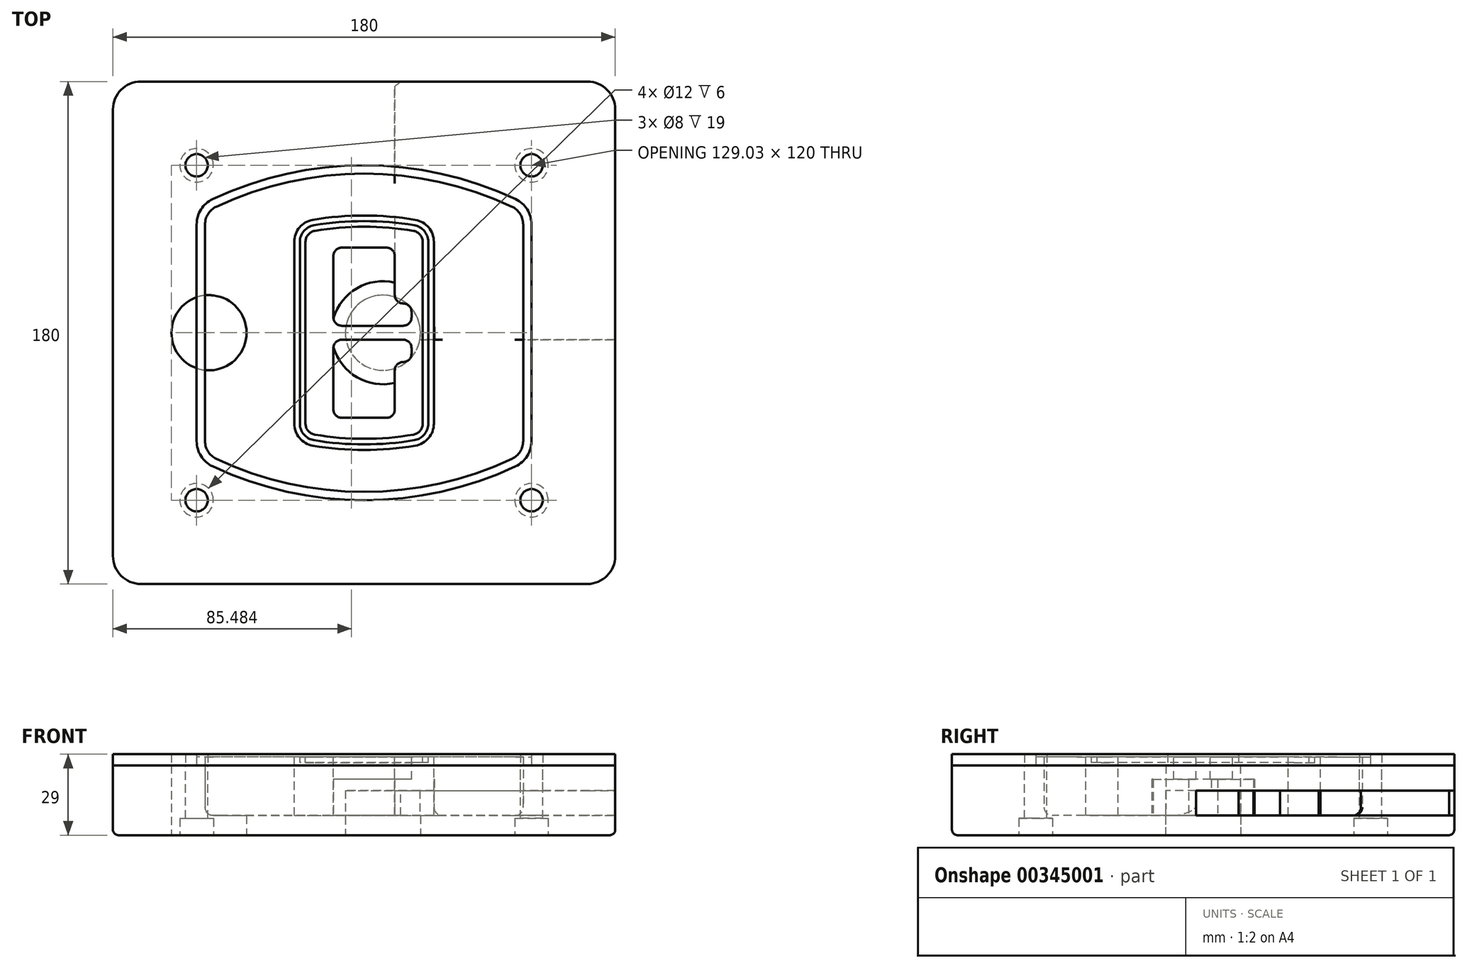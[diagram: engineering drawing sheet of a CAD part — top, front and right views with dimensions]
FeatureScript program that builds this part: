
annotation { "Feature Type Name" : "Feature", "Feature Type Description" : "" }
export const myFeature = defineFeature(function(context is Context, id is Id, definition is map)
    precondition{}
    {
        {
            var Q0;
            Q0=qCreatedBy(makeId("Top.planeOp"),FACE);
            var sketch = newSketch(context, id + "F0", { "sketchPlane" : qUnion([Q0])});
            skPoint(sketch, "E0.rect.middle", {"position": v(0, 0) * mm});
            skLineSegment(sketch, "E1.bottom", {"start": v(-80, -90) * mm, "end": v(80, -90) * mm});
            skLineSegment(sketch, "E1.top", {"start": v(-80, 90) * mm, "end": v(80, 90) * mm});
            skLineSegment(sketch, "E1.left", {"start": v(-90, -80) * mm, "end": v(-90, 80) * mm});
            skLineSegment(sketch, "E1.right", {"start": v(90, -80) * mm, "end": v(90, 80) * mm});
            skLineSegment(sketch, "E2", {"start": v(-90, 90) * mm, "end": v(90, -90) * mm, "construction": true});
            skLineSegment(sketch, "E3", {"start": v(90, 90) * mm, "end": v(-90, -90) * mm, "construction": true});
            skCircle(sketch, "E4", {"center": v(-60, 60) * mm, "radius": 4 * mm});
            skCircle(sketch, "E5", {"center": v(60, 60) * mm, "radius": 4 * mm});
            skCircle(sketch, "E6", {"center": v(60, -60) * mm, "radius": 4 * mm});
            skCircle(sketch, "E7", {"center": v(-60, -60) * mm, "radius": 4 * mm});
            skLineSegment(sketch, "E8", {"start": v(-60, 60) * mm, "end": v(60, 60) * mm, "construction": true});
            skLineSegment(sketch, "E9", {"start": v(60, 60) * mm, "end": v(60, -60) * mm, "construction": true});
            skLineSegment(sketch, "E10", {"start": v(60, -60) * mm, "end": v(-60, -60) * mm, "construction": true});
            skLineSegment(sketch, "E11", {"start": v(-60, -60) * mm, "end": v(-60, 60) * mm, "construction": true});
            skLineSegment(sketch, "E12", {"start": v(-60, 38.83) * mm, "end": v(-60, -38.83) * mm});
            skLineSegment(sketch, "E13", {"start": v(60, 38.83) * mm, "end": v(60, -38.83) * mm});
            skArc(sketch, "E14", {"start": v(54.26, 47.88) * mm, "mid": v(0, 60) * mm, "end": v(-54.26, 47.88) * mm});
            skArc(sketch, "E15", {"start": v(-54.26, -47.88) * mm, "mid": v(0, -60) * mm, "end": v(54.26, -47.88) * mm});
            skLineSegment(sketch, "E16", {"start": v(-60, 0) * mm, "end": v(60, 0) * mm, "construction": true});
            skPoint(sketch, "E17.visualSharp", {"position": v(-60, -45) * mm});
            skArc(sketch, "E17.filletArc", {"start": v(-60, -38.83) * mm, "mid": v(-58.44, -44.2) * mm, "end": v(-54.26, -47.88) * mm});
            skPoint(sketch, "E18.visualSharp", {"position": v(-60, 45) * mm});
            skArc(sketch, "E18.filletArc", {"start": v(-54.26, 47.88) * mm, "mid": v(-58.44, 44.2) * mm, "end": v(-60, 38.83) * mm});
            skPoint(sketch, "E19.visualSharp", {"position": v(60, 45) * mm});
            skArc(sketch, "E19.filletArc", {"start": v(60, 38.83) * mm, "mid": v(58.44, 44.2) * mm, "end": v(54.26, 47.88) * mm});
            skPoint(sketch, "E20.visualSharp", {"position": v(60, -45) * mm});
            skArc(sketch, "E20.filletArc", {"start": v(54.26, -47.88) * mm, "mid": v(58.44, -44.2) * mm, "end": v(60, -38.83) * mm});
            skPoint(sketch, "E21.visualSharp", {"position": v(-90, 90) * mm});
            skArc(sketch, "E21.filletArc", {"start": v(-80, 90) * mm, "mid": v(-87.07, 87.07) * mm, "end": v(-90, 80) * mm});
            skPoint(sketch, "E22.visualSharp", {"position": v(90, 90) * mm});
            skArc(sketch, "E22.filletArc", {"start": v(90, 80) * mm, "mid": v(87.07, 87.07) * mm, "end": v(80, 90) * mm});
            skPoint(sketch, "E23.visualSharp", {"position": v(90, -90) * mm});
            skArc(sketch, "E23.filletArc", {"start": v(80, -90) * mm, "mid": v(87.07, -87.07) * mm, "end": v(90, -80) * mm});
            skPoint(sketch, "E24.visualSharp", {"position": v(-90, -90) * mm});
            skArc(sketch, "E24.filletArc", {"start": v(-90, -80) * mm, "mid": v(-87.07, -87.07) * mm, "end": v(-80, -90) * mm});
            skArc(sketch, "E25.0", {"start": v(57, 38.83) * mm, "mid": v(55.9, 42.58) * mm, "end": v(52.98, 45.17) * mm});
            skLineSegment(sketch, "E25.1", {"start": v(57, 38.83) * mm, "end": v(57, -38.83) * mm});
            skArc(sketch, "E25.2", {"start": v(52.98, -45.17) * mm, "mid": v(55.9, -42.58) * mm, "end": v(57, -38.83) * mm});
            skArc(sketch, "E25.3", {"start": v(-52.98, -45.17) * mm, "mid": v(0, -57) * mm, "end": v(52.98, -45.17) * mm});
            skArc(sketch, "E25.4", {"start": v(-57, -38.83) * mm, "mid": v(-55.9, -42.58) * mm, "end": v(-52.98, -45.17) * mm});
            skArc(sketch, "E25.5", {"start": v(52.98, 45.17) * mm, "mid": v(0, 57) * mm, "end": v(-52.98, 45.17) * mm});
            skLineSegment(sketch, "E25.6", {"start": v(-57, 38.83) * mm, "end": v(-57, -38.83) * mm});
            skArc(sketch, "E25.7", {"start": v(-52.98, 45.17) * mm, "mid": v(-55.9, 42.58) * mm, "end": v(-57, 38.83) * mm});
            skArc(sketch, "E26.0", {"start": v(-55.96, 51.5) * mm, "mid": v(-61.82, 46.33) * mm, "end": v(-64, 38.83) * mm});
            skArc(sketch, "E26.1", {"start": v(55.96, 51.5) * mm, "mid": v(0, 64) * mm, "end": v(-55.96, 51.5) * mm});
            skArc(sketch, "E26.2", {"start": v(64, 38.83) * mm, "mid": v(61.82, 46.33) * mm, "end": v(55.96, 51.5) * mm});
            skLineSegment(sketch, "E26.3", {"start": v(64, 38.83) * mm, "end": v(64, -38.83) * mm});
            skArc(sketch, "E26.4", {"start": v(55.96, -51.5) * mm, "mid": v(61.82, -46.33) * mm, "end": v(64, -38.83) * mm});
            skLineSegment(sketch, "E26.5", {"start": v(-64, 38.83) * mm, "end": v(-64, -38.83) * mm});
            skArc(sketch, "E26.6", {"start": v(-55.96, -51.5) * mm, "mid": v(0, -64) * mm, "end": v(55.96, -51.5) * mm});
            skArc(sketch, "E26.7", {"start": v(-64, -38.83) * mm, "mid": v(-61.82, -46.33) * mm, "end": v(-55.96, -51.5) * mm});
            skSolve(sketch);
        }
        {
            var Q0;
            Q0=makeQuery(id+"F0.imprint","IMPRINT",FACE,{"disambiguationData":[TD([[makeQuery(id+"F0.imprint","IMPRINT",EDGE,{"derivedFrom":sQuery(id+"F0.wireOp",EDGE,"E1.bottom")}),1.0]])]});
            var Q1;
            Q1=makeQuery(id+"F0.imprint","IMPRINT",FACE,{"disambiguationData":[TD([[makeQuery(id+"F0.imprint","IMPRINT",EDGE,{"derivedFrom":sQuery(id+"F0.wireOp",EDGE,"E12")}),1.0]])]});
            var Q2;
            Q2=makeQuery(id+"F0.imprint","IMPRINT",FACE,{"disambiguationData":[TD([[makeQuery(id+"F0.imprint","IMPRINT",EDGE,{"derivedFrom":sQuery(id+"F0.wireOp",EDGE,"E25.0")}),1.0]])]});
            var Q3;
            Q3=makeQuery(id+"F0.imprint","IMPRINT",FACE,{"disambiguationData":[TD([[makeQuery(id+"F0.imprint","IMPRINT",EDGE,{"derivedFrom":sQuery(id+"F0.wireOp",EDGE,"E12")}),-1.0]])]});
            extrude(context, id + "F1", {"entities" : qUnion([Q0, Q1, Q2, Q3]), "oppositeDirection" : true, "depth" : 25 * mm});
        }
        {
            var Q0;
            Q0=makeQuery(id+"F0.imprint","IMPRINT",FACE,{"disambiguationData":[TD([[makeQuery(id+"F0.imprint","IMPRINT",EDGE,{"derivedFrom":sQuery(id+"F0.wireOp",EDGE,"E12")}),1.0]])]});
            extrude(context, id + "F2", {"entities" : qUnion([Q0]), "operationType" : NewBodyOperationType.ADD, "depth" : 3 * mm});
        }
        {
            var Q0;
            Q0=makeQuery(id+"F0.imprint","IMPRINT",FACE,{"disambiguationData":[TD([[makeQuery(id+"F0.imprint","IMPRINT",EDGE,{"derivedFrom":sQuery(id+"F0.wireOp",EDGE,"E25.0")}),1.0]])]});
            extrude(context, id + "F3", {"entities" : qUnion([Q0]), "operationType" : NewBodyOperationType.REMOVE, "oppositeDirection" : true, "depth" : 18 * mm});
        }
        {
            var Q0;
            Q0=makeQuery(id+"F2.opExtrude","CAP_FACE",FACE,{"disambiguationData":[OSD([sQuery(id+"F0.wireOp",EDGE,"E12"),sQuery(id+"F0.wireOp",EDGE,"E13"),sQuery(id+"F0.wireOp",EDGE,"E14"),sQuery(id+"F0.wireOp",EDGE,"E15"),sQuery(id+"F0.wireOp",EDGE,"E17.filletArc"),sQuery(id+"F0.wireOp",EDGE,"E18.filletArc"),sQuery(id+"F0.wireOp",EDGE,"E19.filletArc"),sQuery(id+"F0.wireOp",EDGE,"E20.filletArc"),sQuery(id+"F0.wireOp",EDGE,"E25.0"),sQuery(id+"F0.wireOp",EDGE,"E25.1"),sQuery(id+"F0.wireOp",EDGE,"E25.2"),sQuery(id+"F0.wireOp",EDGE,"E25.3"),sQuery(id+"F0.wireOp",EDGE,"E25.4"),sQuery(id+"F0.wireOp",EDGE,"E25.5"),sQuery(id+"F0.wireOp",EDGE,"E25.6"),sQuery(id+"F0.wireOp",EDGE,"E25.7")])],"isStart":false});
            var sketch = newSketch(context, id + "F4", { "sketchPlane" : qUnion([Q0])});
            skArc(sketch, "E27.0", {"start": v(-18.34, -40.45) * mm, "mid": v(0, -42) * mm, "end": v(18.34, -40.45) * mm});
            skArc(sketch, "E28.0", {"start": v(18.34, 40.45) * mm, "mid": v(0, 42) * mm, "end": v(-18.34, 40.45) * mm});
            skLineSegment(sketch, "E29", {"start": v(-25, 32.57) * mm, "end": v(-25, -32.57) * mm});
            skLineSegment(sketch, "E30", {"start": v(25, 32.57) * mm, "end": v(25, -32.57) * mm});
            skLineSegment(sketch, "E31", {"start": v(-25, 39.1) * mm, "end": v(25, 39.1) * mm, "construction": true});
            skLineSegment(sketch, "E32", {"start": v(-25, -39.1) * mm, "end": v(25, -39.1) * mm, "construction": true});
            skPoint(sketch, "E33.visualSharp", {"position": v(-25, 39.1) * mm});
            skArc(sketch, "E33.filletArc", {"start": v(-18.34, 40.45) * mm, "mid": v(-23.11, 37.73) * mm, "end": v(-25, 32.57) * mm});
            skPoint(sketch, "E34.visualSharp", {"position": v(25, 39.1) * mm});
            skArc(sketch, "E34.filletArc", {"start": v(25, 32.57) * mm, "mid": v(23.11, 37.73) * mm, "end": v(18.34, 40.45) * mm});
            skPoint(sketch, "E35.visualSharp", {"position": v(25, -39.1) * mm});
            skArc(sketch, "E35.filletArc", {"start": v(18.34, -40.45) * mm, "mid": v(23.11, -37.73) * mm, "end": v(25, -32.57) * mm});
            skPoint(sketch, "E36.visualSharp", {"position": v(-25, -39.1) * mm});
            skArc(sketch, "E36.filletArc", {"start": v(-25, -32.57) * mm, "mid": v(-23.11, -37.73) * mm, "end": v(-18.34, -40.45) * mm});
            skArc(sketch, "E37.0", {"start": v(52.98, 45.17) * mm, "mid": v(0, 57) * mm, "end": v(-52.98, 45.17) * mm});
            skArc(sketch, "E37.1", {"start": v(-52.98, 45.17) * mm, "mid": v(-55.9, 42.58) * mm, "end": v(-57, 38.83) * mm});
            skLineSegment(sketch, "E37.2", {"start": v(-57, 38.83) * mm, "end": v(-57, -38.83) * mm});
            skArc(sketch, "E37.3", {"start": v(-57, -38.83) * mm, "mid": v(-55.9, -42.58) * mm, "end": v(-52.98, -45.17) * mm});
            skArc(sketch, "E37.4", {"start": v(-52.98, -45.17) * mm, "mid": v(0, -57) * mm, "end": v(52.98, -45.17) * mm});
            skArc(sketch, "E37.5", {"start": v(52.98, -45.17) * mm, "mid": v(55.9, -42.58) * mm, "end": v(57, -38.83) * mm});
            skLineSegment(sketch, "E37.6", {"start": v(57, 38.83) * mm, "end": v(57, -38.83) * mm});
            skArc(sketch, "E37.7", {"start": v(57, 38.83) * mm, "mid": v(55.9, 42.58) * mm, "end": v(52.98, 45.17) * mm});
            skLineSegment(sketch, "E38.0", {"start": v(23, 32.57) * mm, "end": v(23, -32.57) * mm});
            skArc(sketch, "E38.1", {"start": v(18, -38.48) * mm, "mid": v(21.58, -36.44) * mm, "end": v(23, -32.57) * mm});
            skArc(sketch, "E38.2", {"start": v(-18, -38.48) * mm, "mid": v(0, -40) * mm, "end": v(18, -38.48) * mm});
            skArc(sketch, "E38.3", {"start": v(-23, -32.57) * mm, "mid": v(-21.58, -36.44) * mm, "end": v(-18, -38.48) * mm});
            skLineSegment(sketch, "E38.4", {"start": v(-23, 32.57) * mm, "end": v(-23, -32.57) * mm});
            skArc(sketch, "E38.5", {"start": v(23, 32.57) * mm, "mid": v(21.58, 36.44) * mm, "end": v(18, 38.48) * mm});
            skArc(sketch, "E38.6", {"start": v(-18, 38.48) * mm, "mid": v(-21.58, 36.44) * mm, "end": v(-23, 32.57) * mm});
            skArc(sketch, "E38.7", {"start": v(18, 38.48) * mm, "mid": v(0, 40) * mm, "end": v(-18, 38.48) * mm});
            skArc(sketch, "E39.0", {"start": v(21, 32.57) * mm, "mid": v(20.06, 35.15) * mm, "end": v(17.67, 36.5) * mm});
            skLineSegment(sketch, "E39.1", {"start": v(21, 32.57) * mm, "end": v(21, -32.57) * mm});
            skArc(sketch, "E39.2", {"start": v(17.67, -36.5) * mm, "mid": v(20.06, -35.15) * mm, "end": v(21, -32.57) * mm});
            skArc(sketch, "E39.3", {"start": v(-17.67, -36.5) * mm, "mid": v(0, -38) * mm, "end": v(17.67, -36.5) * mm});
            skArc(sketch, "E39.4", {"start": v(-21, -32.57) * mm, "mid": v(-20.06, -35.15) * mm, "end": v(-17.67, -36.5) * mm});
            skArc(sketch, "E39.5", {"start": v(17.67, 36.5) * mm, "mid": v(0, 38) * mm, "end": v(-17.67, 36.5) * mm});
            skLineSegment(sketch, "E39.6", {"start": v(-21, 32.57) * mm, "end": v(-21, -32.57) * mm});
            skArc(sketch, "E39.7", {"start": v(-17.67, 36.5) * mm, "mid": v(-20.06, 35.15) * mm, "end": v(-21, 32.57) * mm});
            skLineSegment(sketch, "E40", {"start": v(-25, 0) * mm, "end": v(25, 0) * mm, "construction": true});
            skLineSegment(sketch, "E41", {"start": v(-11, 5.5) * mm, "end": v(-11, 27.5) * mm});
            skLineSegment(sketch, "E42", {"start": v(-8, 30.5) * mm, "end": v(8, 30.5) * mm});
            skLineSegment(sketch, "E43", {"start": v(11, 27.5) * mm, "end": v(11, 13.5) * mm});
            skLineSegment(sketch, "E44", {"start": v(14, 10.5) * mm, "end": v(14, 10.5) * mm});
            skLineSegment(sketch, "E45", {"start": v(17, 7.5) * mm, "end": v(17, 5.5) * mm});
            skLineSegment(sketch, "E46", {"start": v(14, 2.5) * mm, "end": v(-8, 2.5) * mm});
            skPoint(sketch, "E47.visualSharp", {"position": v(-11, 30.5) * mm});
            skArc(sketch, "E47.filletArc", {"start": v(-8, 30.5) * mm, "mid": v(-10.12, 29.62) * mm, "end": v(-11, 27.5) * mm});
            skPoint(sketch, "E48.visualSharp", {"position": v(11, 30.5) * mm});
            skArc(sketch, "E48.filletArc", {"start": v(11, 27.5) * mm, "mid": v(10.12, 29.62) * mm, "end": v(8, 30.5) * mm});
            skPoint(sketch, "E49.visualSharp", {"position": v(11, 10.5) * mm});
            skArc(sketch, "E49.filletArc", {"start": v(11, 13.5) * mm, "mid": v(11.88, 11.38) * mm, "end": v(14, 10.5) * mm});
            skPoint(sketch, "E50.visualSharp", {"position": v(17, 10.5) * mm});
            skArc(sketch, "E50.filletArc", {"start": v(17, 7.5) * mm, "mid": v(16.12, 9.62) * mm, "end": v(14, 10.5) * mm});
            skPoint(sketch, "E51.visualSharp", {"position": v(17, 2.5) * mm});
            skArc(sketch, "E51.filletArc", {"start": v(14, 2.5) * mm, "mid": v(16.12, 3.38) * mm, "end": v(17, 5.5) * mm});
            skPoint(sketch, "E52.visualSharp", {"position": v(-11, 2.5) * mm});
            skArc(sketch, "E52.filletArc", {"start": v(-11, 5.5) * mm, "mid": v(-10.12, 3.38) * mm, "end": v(-8, 2.5) * mm});
            skLineSegment(sketch, "E53.0.MirrorCS", {"start": v(14, -2.5) * mm, "end": v(-8, -2.5) * mm});
            skArc(sketch, "E54.0.MirrorCS", {"start": v(-11, -5.5) * mm, "mid": v(-10.12, -3.38) * mm, "end": v(-8, -2.5) * mm});
            skLineSegment(sketch, "E55.0.MirrorCS", {"start": v(-11, -5.5) * mm, "end": v(-11, -27.5) * mm});
            skArc(sketch, "E56.0.MirrorCS", {"start": v(-8, -30.5) * mm, "mid": v(-10.12, -29.62) * mm, "end": v(-11, -27.5) * mm});
            skLineSegment(sketch, "E57.0.MirrorCS", {"start": v(-8, -30.5) * mm, "end": v(8, -30.5) * mm});
            skArc(sketch, "E58.0.MirrorCS", {"start": v(11, -27.5) * mm, "mid": v(10.12, -29.62) * mm, "end": v(8, -30.5) * mm});
            skLineSegment(sketch, "E59.0.MirrorCS", {"start": v(11, -27.5) * mm, "end": v(11, -13.5) * mm});
            skArc(sketch, "E60.0.MirrorCS", {"start": v(11, -13.5) * mm, "mid": v(11.88, -11.38) * mm, "end": v(14, -10.5) * mm});
            skArc(sketch, "E61.0.MirrorCS", {"start": v(17, -7.5) * mm, "mid": v(16.12, -9.62) * mm, "end": v(14, -10.5) * mm});
            skLineSegment(sketch, "E62.0.MirrorCS", {"start": v(17, -7.5) * mm, "end": v(17, -5.5) * mm});
            skArc(sketch, "E63.0.MirrorCS", {"start": v(14, -2.5) * mm, "mid": v(16.12, -3.38) * mm, "end": v(17, -5.5) * mm});
            skSolve(sketch);
        }
        {
            var Q0;
            Q0=makeQuery(id+"F4.imprint","IMPRINT",FACE,{"disambiguationData":[TD([[makeQuery(id+"F4.imprint","IMPRINT",EDGE,{"derivedFrom":sQuery(id+"F4.wireOp",EDGE,"E27.0")}),1.0]])]});
            var Q1;
            Q1=makeQuery(id+"F4.imprint","IMPRINT",FACE,{"disambiguationData":[TD([[makeQuery(id+"F4.imprint","IMPRINT",EDGE,{"derivedFrom":sQuery(id+"F4.wireOp",EDGE,"E38.0")}),-1.0]])]});
            var Q2;
            Q2=makeQuery(id+"F4.imprint","IMPRINT",FACE,{"disambiguationData":[TD([[makeQuery(id+"F4.imprint","IMPRINT",EDGE,{"derivedFrom":sQuery(id+"F4.wireOp",EDGE,"E39.0")}),1.0]])]});
            extrude(context, id + "F5", {"entities" : qUnion([Q0, Q1, Q2]), "operationType" : NewBodyOperationType.ADD, "endBound" : BoundingType.UP_TO_NEXT, "oppositeDirection" : true, "depth" : 25 * mm});
        }
        {
            var Q0;
            Q0=makeQuery(id+"F4.imprint","IMPRINT",FACE,{"disambiguationData":[TD([[makeQuery(id+"F4.imprint","IMPRINT",EDGE,{"derivedFrom":sQuery(id+"F4.wireOp",EDGE,"E38.0")}),-1.0]])]});
            extrude(context, id + "F6", {"entities" : qUnion([Q0]), "operationType" : NewBodyOperationType.REMOVE, "oppositeDirection" : true, "depth" : 2 * mm});
        }
        {
            var Q0;
            Q0=makeQuery(id+"F1.opExtrude","CAP_FACE",FACE,{"disambiguationData":[OSD([sQuery(id+"F0.wireOp",EDGE,"E1.bottom"),sQuery(id+"F0.wireOp",EDGE,"E1.top"),sQuery(id+"F0.wireOp",EDGE,"E1.left"),sQuery(id+"F0.wireOp",EDGE,"E1.right"),sQuery(id+"F0.wireOp",EDGE,"E4"),sQuery(id+"F0.wireOp",EDGE,"E5"),sQuery(id+"F0.wireOp",EDGE,"E6"),sQuery(id+"F0.wireOp",EDGE,"E7"),sQuery(id+"F0.wireOp",EDGE,"E21.filletArc"),sQuery(id+"F0.wireOp",EDGE,"E22.filletArc"),sQuery(id+"F0.wireOp",EDGE,"E23.filletArc"),sQuery(id+"F0.wireOp",EDGE,"E24.filletArc")])],"isStart":false});
            var sketch = newSketch(context, id + "F7", { "sketchPlane" : qUnion([Q0])});
            skCircle(sketch, "E64", {"center": v(6.76, 0) * mm, "radius": 13.47 * mm});
            skCircle(sketch, "E65", {"center": v(-55.56, 0) * mm, "radius": 13.47 * mm});
            skLineSegment(sketch, "E66", {"start": v(90, 0) * mm, "end": v(-90, 0) * mm});
            skCircle(sketch, "E67", {"center": v(6.76, 0) * mm, "radius": 18.47 * mm});
            skCircle(sketch, "E68", {"center": v(60, -60) * mm, "radius": 6 * mm});
            skCircle(sketch, "E69", {"center": v(-60, -60) * mm, "radius": 6 * mm});
            skCircle(sketch, "E70", {"center": v(-60, 60) * mm, "radius": 6 * mm});
            skCircle(sketch, "E71", {"center": v(60, 60) * mm, "radius": 6 * mm});
            skSolve(sketch);
        }
        {
            var Q0;
            {var subQ1=sQuery(id+"F7.wireOp",EDGE,"E66");var subQ4=sQuery(id+"F7.wireOp",EDGE,"E64");var subQ6=makeQuery(id+"F7.imprint","INTERSECT",VERTEX,{"disambiguationData":[OD(0.0)],"derivedFrom":[subQ4,subQ1]});Q0=makeQuery(id+"F7.imprint","IMPRINT",FACE,{"disambiguationData":[TD([[makeQuery(id+"F7.imprint","IMPRINT",EDGE,{"disambiguationData":[TD([[subQ6,-1.0]])],"derivedFrom":subQ4}),-1.0]])]});}
            var Q1;
            {var subQ0=sQuery(id+"F7.wireOp",EDGE,"E66");var subQ1=sQuery(id+"F7.wireOp",EDGE,"E64");var subQ3=makeQuery(id+"F7.imprint","INTERSECT",VERTEX,{"disambiguationData":[OD(0.0)],"derivedFrom":[subQ1,subQ0]});Q1=makeQuery(id+"F7.imprint","IMPRINT",FACE,{"disambiguationData":[TD([[makeQuery(id+"F7.imprint","IMPRINT",EDGE,{"disambiguationData":[TD([[subQ3,-1.0]])],"derivedFrom":subQ1}),1.0]])]});}
            var Q2;
            {var subQ0=sQuery(id+"F7.wireOp",EDGE,"E66");var subQ1=sQuery(id+"F7.wireOp",EDGE,"E64");var subQ3=makeQuery(id+"F7.imprint","INTERSECT",VERTEX,{"disambiguationData":[OD(0.0)],"derivedFrom":[subQ1,subQ0]});Q2=makeQuery(id+"F7.imprint","IMPRINT",FACE,{"disambiguationData":[TD([[makeQuery(id+"F7.imprint","IMPRINT",EDGE,{"disambiguationData":[TD([[subQ3,1.0]])],"derivedFrom":subQ1}),1.0]])]});}
            var Q3;
            {var subQ1=sQuery(id+"F7.wireOp",EDGE,"E66");var subQ4=sQuery(id+"F7.wireOp",EDGE,"E64");var subQ6=makeQuery(id+"F7.imprint","INTERSECT",VERTEX,{"disambiguationData":[OD(0.0)],"derivedFrom":[subQ4,subQ1]});Q3=makeQuery(id+"F7.imprint","IMPRINT",FACE,{"disambiguationData":[TD([[makeQuery(id+"F7.imprint","IMPRINT",EDGE,{"disambiguationData":[TD([[subQ6,1.0]])],"derivedFrom":subQ4}),-1.0]])]});}
            extrude(context, id + "F8", {"entities" : qUnion([Q0, Q1, Q2, Q3]), "operationType" : NewBodyOperationType.ADD, "oppositeDirection" : true, "depth" : 20 * mm});
        }
        {
            var Q0;
            {var subQ0=sQuery(id+"F7.wireOp",EDGE,"E66");var subQ1=sQuery(id+"F7.wireOp",EDGE,"E64");var subQ3=makeQuery(id+"F7.imprint","INTERSECT",VERTEX,{"disambiguationData":[OD(0.0)],"derivedFrom":[subQ1,subQ0]});Q0=makeQuery(id+"F7.imprint","IMPRINT",FACE,{"disambiguationData":[TD([[makeQuery(id+"F7.imprint","IMPRINT",EDGE,{"disambiguationData":[TD([[subQ3,-1.0]])],"derivedFrom":subQ1}),1.0]])]});}
            var Q1;
            {var subQ0=sQuery(id+"F7.wireOp",EDGE,"E66");var subQ1=sQuery(id+"F7.wireOp",EDGE,"E64");var subQ3=makeQuery(id+"F7.imprint","INTERSECT",VERTEX,{"disambiguationData":[OD(0.0)],"derivedFrom":[subQ1,subQ0]});Q1=makeQuery(id+"F7.imprint","IMPRINT",FACE,{"disambiguationData":[TD([[makeQuery(id+"F7.imprint","IMPRINT",EDGE,{"disambiguationData":[TD([[subQ3,1.0]])],"derivedFrom":subQ1}),1.0]])]});}
            extrude(context, id + "F9", {"entities" : qUnion([Q0, Q1]), "operationType" : NewBodyOperationType.REMOVE, "oppositeDirection" : true, "depth" : 16 * mm});
        }
        {
            var Q0;
            {var subQ0=sQuery(id+"F7.wireOp",EDGE,"E66");var subQ1=sQuery(id+"F7.wireOp",EDGE,"E65");var subQ3=makeQuery(id+"F7.imprint","INTERSECT",VERTEX,{"disambiguationData":[OD(0.0)],"derivedFrom":[subQ1,subQ0]});Q0=makeQuery(id+"F7.imprint","IMPRINT",FACE,{"disambiguationData":[TD([[makeQuery(id+"F7.imprint","IMPRINT",EDGE,{"disambiguationData":[TD([[subQ3,-1.0]])],"derivedFrom":subQ1}),1.0]])]});}
            var Q1;
            {var subQ0=sQuery(id+"F7.wireOp",EDGE,"E66");var subQ1=sQuery(id+"F7.wireOp",EDGE,"E65");var subQ3=makeQuery(id+"F7.imprint","INTERSECT",VERTEX,{"disambiguationData":[OD(0.0)],"derivedFrom":[subQ1,subQ0]});Q1=makeQuery(id+"F7.imprint","IMPRINT",FACE,{"disambiguationData":[TD([[makeQuery(id+"F7.imprint","IMPRINT",EDGE,{"disambiguationData":[TD([[subQ3,1.0]])],"derivedFrom":subQ1}),1.0]])]});}
            extrude(context, id + "F10", {"entities" : qUnion([Q0, Q1]), "operationType" : NewBodyOperationType.REMOVE, "oppositeDirection" : true, "depth" : 25 * mm});
        }
        {
            var Q0;
            Q0=makeQuery(id+"F7.imprint","IMPRINT",FACE,{"disambiguationData":[TD([[makeQuery(id+"F7.imprint","IMPRINT",EDGE,{"derivedFrom":sQuery(id+"F7.wireOp",EDGE,"E68")}),1.0]])]});
            var Q1;
            Q1=makeQuery(id+"F7.imprint","IMPRINT",FACE,{"disambiguationData":[TD([[makeQuery(id+"F7.imprint","IMPRINT",EDGE,{"derivedFrom":makeQuery(id+"F1.opExtrude","CAP_EDGE",EDGE,{"disambiguationData":[OSD([sQuery(id+"F0.wireOp",EDGE,"E5")])],"isStart":false})}),-1.0]])]});
            var Q2;
            Q2=makeQuery(id+"F7.imprint","IMPRINT",FACE,{"disambiguationData":[TD([[makeQuery(id+"F7.imprint","IMPRINT",EDGE,{"derivedFrom":sQuery(id+"F7.wireOp",EDGE,"E69")}),1.0]])]});
            var Q3;
            Q3=makeQuery(id+"F7.imprint","IMPRINT",FACE,{"disambiguationData":[TD([[makeQuery(id+"F7.imprint","IMPRINT",EDGE,{"derivedFrom":makeQuery(id+"F1.opExtrude","CAP_EDGE",EDGE,{"disambiguationData":[OSD([sQuery(id+"F0.wireOp",EDGE,"E4")])],"isStart":false})}),-1.0]])]});
            var Q4;
            Q4=makeQuery(id+"F7.imprint","IMPRINT",FACE,{"disambiguationData":[TD([[makeQuery(id+"F7.imprint","IMPRINT",EDGE,{"derivedFrom":sQuery(id+"F7.wireOp",EDGE,"E70")}),1.0]])]});
            var Q5;
            Q5=makeQuery(id+"F7.imprint","IMPRINT",FACE,{"disambiguationData":[TD([[makeQuery(id+"F7.imprint","IMPRINT",EDGE,{"derivedFrom":makeQuery(id+"F1.opExtrude","CAP_EDGE",EDGE,{"disambiguationData":[OSD([sQuery(id+"F0.wireOp",EDGE,"E7")])],"isStart":false})}),-1.0]])]});
            var Q6;
            Q6=makeQuery(id+"F7.imprint","IMPRINT",FACE,{"disambiguationData":[TD([[makeQuery(id+"F7.imprint","IMPRINT",EDGE,{"derivedFrom":sQuery(id+"F7.wireOp",EDGE,"E71")}),1.0]])]});
            var Q7;
            Q7=makeQuery(id+"F7.imprint","IMPRINT",FACE,{"disambiguationData":[TD([[makeQuery(id+"F7.imprint","IMPRINT",EDGE,{"derivedFrom":makeQuery(id+"F1.opExtrude","CAP_EDGE",EDGE,{"disambiguationData":[OSD([sQuery(id+"F0.wireOp",EDGE,"E6")])],"isStart":false})}),-1.0]])]});
            extrude(context, id + "F11", {"entities" : qUnion([Q0, Q1, Q2, Q3, Q4, Q5, Q6, Q7]), "operationType" : NewBodyOperationType.REMOVE, "oppositeDirection" : true, "depth" : 6 * mm});
        }
        {
            var Q0;
            Q0=makeQuery(id+"F9.boolean.opBoolean","COPY",FACE,{"derivedFrom":makeQuery(id+"F9.opExtrude","CAP_FACE",FACE,{"disambiguationData":[OSD([sQuery(id+"F7.wireOp",EDGE,"E64")])],"isStart":false})});
            var sketch = newSketch(context, id + "F12", { "sketchPlane" : qUnion([Q0])});
            skArc(sketch, "E72.0", {"start": v(11, -88.19) * mm, "mid": v(97.1, -83.6) * mm, "end": v(92.5, 2.5) * mm});
            skLineSegment(sketch, "E72.1", {"start": v(11, -17.97) * mm, "end": v(11, -17.97) * mm});
            skLineSegment(sketch, "E73", {"start": v(92.5, -105.13) * mm, "end": v(102.3, -105.13) * mm});
            skLineSegment(sketch, "E74.0", {"start": v(92.5, 2.5) * mm, "end": v(14, 2.5) * mm});
            skArc(sketch, "E74.1", {"start": v(14, 2.5) * mm, "mid": v(16.12, 3.38) * mm, "end": v(17, 5.5) * mm});
            skLineSegment(sketch, "E74.2", {"start": v(17, 7.5) * mm, "end": v(17, 5.5) * mm});
            skArc(sketch, "E74.3", {"start": v(17, 7.5) * mm, "mid": v(16.12, 9.62) * mm, "end": v(14, 10.5) * mm});
            skArc(sketch, "E74.4", {"start": v(11, 13.5) * mm, "mid": v(11.88, 11.38) * mm, "end": v(14, 10.5) * mm});
            skLineSegment(sketch, "E74.5", {"start": v(11, 13.5) * mm, "end": v(11, -88.19) * mm});
            skLineSegment(sketch, "E74.7", {"start": v(92.5, -2.5) * mm, "end": v(14, -2.5) * mm});
            skArc(sketch, "E74.8", {"start": v(14, -2.5) * mm, "mid": v(16.12, -3.38) * mm, "end": v(17, -5.5) * mm});
            skLineSegment(sketch, "E74.9", {"start": v(17, -7.5) * mm, "end": v(17, -5.5) * mm});
            skArc(sketch, "E74.10", {"start": v(17, -7.5) * mm, "mid": v(16.12, -9.62) * mm, "end": v(14, -10.5) * mm});
            skArc(sketch, "E74.11", {"start": v(11, -13.5) * mm, "mid": v(11.88, -11.38) * mm, "end": v(14, -10.5) * mm});
            skLineSegment(sketch, "E74.12", {"start": v(11, -17.97) * mm, "end": v(11, -13.5) * mm});
            skPoint(sketch, "E75.orphan", {"position": v(11, -27.5) * mm});
            skPoint(sketch, "E76.orphan", {"position": v(-8, -2.5) * mm});
            skPoint(sketch, "E77.orphan", {"position": v(-8, 2.5) * mm});
            skPoint(sketch, "E78.orphan", {"position": v(11, 27.5) * mm});
            skSolve(sketch);
        }
        {
            var Q0;
            {var subQ7=sQuery(id+"F12.wireOp",EDGE,"E72.0");var subQ14=sQuery(id+"F12.wireOp",EDGE,"E72.1");var subQ16=sQuery(id+"F12.wireOp",EDGE,"E74.1");var subQ18=sQuery(id+"F12.wireOp",EDGE,"E74.8");Q0=qUnion([makeQuery(id+"F12.imprint","IMPRINT",FACE,{"disambiguationData":[TD([[makeQuery(id+"F12.imprint","IMPRINT",EDGE,{"derivedFrom":subQ7}),1.0]])]}),makeQuery(id+"F12.imprint","IMPRINT",FACE,{"disambiguationData":[TD([[makeQuery(id+"F12.imprint","IMPRINT",EDGE,{"derivedFrom":subQ14}),1.0]])]}),makeQuery(id+"F12.imprint","IMPRINT",FACE,{"disambiguationData":[TD([[makeQuery(id+"F12.imprint","IMPRINT",EDGE,{"derivedFrom":subQ16}),1.0]])]}),makeQuery(id+"F12.imprint","IMPRINT",FACE,{"disambiguationData":[TD([[makeQuery(id+"F12.imprint","IMPRINT",EDGE,{"derivedFrom":subQ18}),-1.0]])]})]);}
            var Q1;
            Q1=makeQuery(id+"F5.boolean.opBoolean","SPLIT",FACE,{"disambiguationData":[TD([makeQuery(id+"F5.opExtrude","SWEPT_FACE",FACE,{"disambiguationData":[OSD([sQuery(id+"F4.wireOp",EDGE,"E41")])]})])],"derivedFrom":makeQuery(id+"F3.boolean.opBoolean","COPY",FACE,{"derivedFrom":makeQuery(id+"F3.opExtrude","CAP_FACE",FACE,{"disambiguationData":[OSD([sQuery(id+"F0.wireOp",EDGE,"E25.0"),sQuery(id+"F0.wireOp",EDGE,"E25.1"),sQuery(id+"F0.wireOp",EDGE,"E25.2"),sQuery(id+"F0.wireOp",EDGE,"E25.3"),sQuery(id+"F0.wireOp",EDGE,"E25.4"),sQuery(id+"F0.wireOp",EDGE,"E25.5"),sQuery(id+"F0.wireOp",EDGE,"E25.6"),sQuery(id+"F0.wireOp",EDGE,"E25.7")])],"isStart":false})})});
            extrude(context, id + "F13", {"entities" : qUnion([Q0]), "operationType" : NewBodyOperationType.REMOVE, "endBound" : BoundingType.UP_TO_SURFACE, "endBoundEntityFace" : qUnion([Q1]), "depth" : 25 * mm});
        }
        {
            var Q0;
            Q0=makeQuery(id+"F3.boolean.opBoolean","COPY",EDGE,{"derivedFrom":makeQuery(id+"F3.opExtrude","CAP_EDGE",EDGE,{"disambiguationData":[OSD([sQuery(id+"F0.wireOp",EDGE,"E25.6")])],"isStart":false})});
            var Q1;
            Q1=makeQuery(id+"F8.boolean.opBoolean","INTERSECT",EDGE,{"derivedFrom":[makeQuery(id+"F5.opExtrude","SWEPT_FACE",FACE,{"disambiguationData":[OSD([sQuery(id+"F4.wireOp",EDGE,"E30")])]}),makeQuery(id+"F8.opExtrude","CAP_FACE",FACE,{"disambiguationData":[OSD([sQuery(id+"F7.wireOp",EDGE,"E67")])],"isStart":false})]});
            var Q2;
            Q2=makeQuery(id+"F8.boolean.opBoolean","INTERSECT",EDGE,{"disambiguationData":[OD(1.0)],"derivedFrom":[makeQuery(id+"F5.opExtrude","SWEPT_FACE",FACE,{"disambiguationData":[OSD([sQuery(id+"F4.wireOp",EDGE,"E30")])]}),makeQuery(id+"F8.opExtrude","SWEPT_FACE",FACE,{"disambiguationData":[OSD([sQuery(id+"F7.wireOp",EDGE,"E67")])]})]});
            var Q3;
            {var subQ0=makeQuery(id+"F3.boolean.opBoolean","COPY",FACE,{"derivedFrom":makeQuery(id+"F3.opExtrude","CAP_FACE",FACE,{"disambiguationData":[OSD([sQuery(id+"F0.wireOp",EDGE,"E25.0"),sQuery(id+"F0.wireOp",EDGE,"E25.1"),sQuery(id+"F0.wireOp",EDGE,"E25.2"),sQuery(id+"F0.wireOp",EDGE,"E25.3"),sQuery(id+"F0.wireOp",EDGE,"E25.4"),sQuery(id+"F0.wireOp",EDGE,"E25.5"),sQuery(id+"F0.wireOp",EDGE,"E25.6"),sQuery(id+"F0.wireOp",EDGE,"E25.7")])],"isStart":false})});var subQ1=sQuery(id+"F4.wireOp",EDGE,"E30");Q3=makeQuery(id+"F8.boolean.opBoolean","SPLIT",EDGE,{"disambiguationData":[TD([makeQuery(id+"F5.opExtrude","SWEPT_FACE",FACE,{"disambiguationData":[OSD([sQuery(id+"F4.wireOp",EDGE,"E35.filletArc")])]})])],"derivedFrom":makeQuery(id+"F5.opExtrude","TWEAK_EDGE",EDGE,{"derivedFrom":[subQ0,makeQuery(id+"F4.imprint","IMPRINT",EDGE,{"derivedFrom":subQ1})]})});}
            var Q4;
            {var subQ0=sQuery(id+"F0.wireOp",EDGE,"E25.0");var subQ1=sQuery(id+"F0.wireOp",EDGE,"E25.1");var subQ2=sQuery(id+"F0.wireOp",EDGE,"E25.2");var subQ3=sQuery(id+"F0.wireOp",EDGE,"E25.3");var subQ4=sQuery(id+"F0.wireOp",EDGE,"E25.4");var subQ5=sQuery(id+"F0.wireOp",EDGE,"E25.5");var subQ6=sQuery(id+"F0.wireOp",EDGE,"E25.6");var subQ7=sQuery(id+"F0.wireOp",EDGE,"E25.7");Q4=makeQuery(id+"F8.boolean.opBoolean","INTERSECT",EDGE,{"derivedFrom":[makeQuery(id+"F5.boolean.opBoolean","SPLIT",FACE,{"disambiguationData":[TD([makeQuery(id+"F2.opExtrude","SWEPT_FACE",FACE,{"disambiguationData":[OSD([subQ0])]})])],"derivedFrom":makeQuery(id+"F3.boolean.opBoolean","COPY",FACE,{"derivedFrom":makeQuery(id+"F3.opExtrude","CAP_FACE",FACE,{"disambiguationData":[OSD([subQ0,subQ1,subQ2,subQ3,subQ4,subQ5,subQ6,subQ7])],"isStart":false})})}),makeQuery(id+"F8.opExtrude","SWEPT_FACE",FACE,{"disambiguationData":[OSD([sQuery(id+"F7.wireOp",EDGE,"E67")])]})]});}
            var Q5;
            Q5=makeQuery(id+"F8.boolean.opBoolean","INTERSECT",EDGE,{"disambiguationData":[OD(0.0)],"derivedFrom":[makeQuery(id+"F5.opExtrude","SWEPT_FACE",FACE,{"disambiguationData":[OSD([sQuery(id+"F4.wireOp",EDGE,"E30")])]}),makeQuery(id+"F8.opExtrude","SWEPT_FACE",FACE,{"disambiguationData":[OSD([sQuery(id+"F7.wireOp",EDGE,"E67")])]})]});
            fillet(context, id + "F14", {"entities" : qUnion([Q0, Q1, Q2, Q3, Q4, Q5]), "radius" : 3 * mm, "tangentPropagation" : true, "allowEdgeOverflow" : false});
        }
        {
            var Q0;
            Q0=makeQuery(id+"F1.opExtrude","CAP_EDGE",EDGE,{"disambiguationData":[OSD([sQuery(id+"F0.wireOp",EDGE,"E1.bottom")])],"isStart":false});
            fillet(context, id + "F15", {"entities" : qUnion([Q0]), "radius" : 2 * mm, "tangentPropagation" : true, "allowEdgeOverflow" : false});
        }
        {
            var Q0;
            {var subQ0=sQuery(id+"F0.wireOp",EDGE,"E21.filletArc");var subQ1=sQuery(id+"F0.wireOp",EDGE,"E7");var subQ2=sQuery(id+"F0.wireOp",EDGE,"E6");var subQ3=sQuery(id+"F0.wireOp",EDGE,"E5");var subQ4=sQuery(id+"F0.wireOp",EDGE,"E4");var subQ5=sQuery(id+"F0.wireOp",EDGE,"E22.filletArc");var subQ6=sQuery(id+"F0.wireOp",EDGE,"E1.bottom");var subQ7=sQuery(id+"F0.wireOp",EDGE,"E1.right");var subQ8=sQuery(id+"F0.wireOp",EDGE,"E1.top");var subQ9=sQuery(id+"F0.wireOp",EDGE,"E1.left");var subQ10=sQuery(id+"F0.wireOp",EDGE,"E23.filletArc");var subQ11=sQuery(id+"F0.wireOp",EDGE,"E24.filletArc");Q0=makeQuery(id+"F2.boolean.opBoolean","SPLIT",FACE,{"disambiguationData":[TD([makeQuery(id+"F1.opExtrude","SWEPT_FACE",FACE,{"disambiguationData":[OSD([subQ6])]})])],"derivedFrom":makeQuery(id+"F1.opExtrude","CAP_FACE",FACE,{"disambiguationData":[OSD([subQ6,subQ8,subQ9,subQ7,subQ4,subQ3,subQ2,subQ1,subQ0,subQ5,subQ10,subQ11])],"isStart":true})});}
            var sketch = newSketch(context, id + "F16", { "sketchPlane" : qUnion([Q0])});
            skLineSegment(sketch, "E79", {"start": v(0, 120) * mm, "end": v(0, 0) * mm, "construction": true});
            skCircle(sketch, "E80", {"center": v(0, 120) * mm, "radius": 6 * mm});
            skLineSegment(sketch, "E81", {"start": v(-15, 108) * mm, "end": v(-15, 119.54) * mm});
            skLineSegment(sketch, "E82", {"start": v(15, 108) * mm, "end": v(15, 119.54) * mm});
            skArc(sketch, "E83", {"start": v(15, 119.54) * mm, "mid": v(0, 135) * mm, "end": v(-15, 119.54) * mm});
            skLineSegment(sketch, "E84", {"start": v(-15, 108) * mm, "end": v(-33, 90) * mm});
            skLineSegment(sketch, "E85", {"start": v(15, 108) * mm, "end": v(33, 90) * mm});
            skArc(sketch, "E86.MirrorCS", {"start": v(-15, 119.54) * mm, "mid": v(0, 135) * mm, "end": v(15, 119.54) * mm});
            skLineSegment(sketch, "E87", {"start": v(0, 0) * mm, "end": v(-138.37, 0) * mm, "construction": true});
            skLineSegment(sketch, "E88", {"start": v(0, 0) * mm, "end": v(115.64, 0) * mm, "construction": true});
            skArc(sketch, "E89.MirrorCS", {"start": v(-15, -119.54) * mm, "mid": v(0, -135) * mm, "end": v(15, -119.54) * mm});
            skLineSegment(sketch, "E90.MirrorCS", {"start": v(-15, -108) * mm, "end": v(-15, -119.54) * mm});
            skLineSegment(sketch, "E91.MirrorCS", {"start": v(-15, -108) * mm, "end": v(-33, -90) * mm});
            skLineSegment(sketch, "E92.MirrorCS", {"start": v(15, -108) * mm, "end": v(33, -90) * mm});
            skLineSegment(sketch, "E93.MirrorCS", {"start": v(0, -120) * mm, "end": v(0, 0) * mm, "construction": true});
            skLineSegment(sketch, "E94.MirrorCS", {"start": v(15, -108) * mm, "end": v(15, -119.54) * mm});
            skCircle(sketch, "E95.MirrorC", {"center": v(0, -120) * mm, "radius": 6 * mm});
            skArc(sketch, "E96.MirrorCS", {"start": v(15, -119.54) * mm, "mid": v(0, -135) * mm, "end": v(-15, -119.54) * mm});
            skSolve(sketch);
        }
        {
            var Q0;
            Q0=makeQuery(id+"F16.imprint","IMPRINT",FACE,{"disambiguationData":[TD([[makeQuery(id+"F16.imprint","IMPRINT",EDGE,{"derivedFrom":sQuery(id+"F16.wireOp",EDGE,"E81")}),-1.0]])]});
            var Q1;
            Q1=makeQuery(id+"F16.imprint","IMPRINT",FACE,{"disambiguationData":[TD([[makeQuery(id+"F16.imprint","IMPRINT",EDGE,{"derivedFrom":makeQuery(id+"F1.opExtrude","CAP_EDGE",EDGE,{"disambiguationData":[OSD([sQuery(id+"F0.wireOp",EDGE,"E1.bottom")])],"isStart":true})}),1.0]])]});
            var Q2;
            Q2=makeQuery(id+"F16.imprint","IMPRINT",FACE,{"disambiguationData":[TD([[makeQuery(id+"F16.imprint","IMPRINT",EDGE,{"derivedFrom":sQuery(id+"F16.wireOp",EDGE,"E95.MirrorC")}),-1.0]])]});
            extrude(context, id + "F17", {"entities" : qUnion([Q0, Q1, Q2]), "depth" : 4 * mm});
        }
    });
